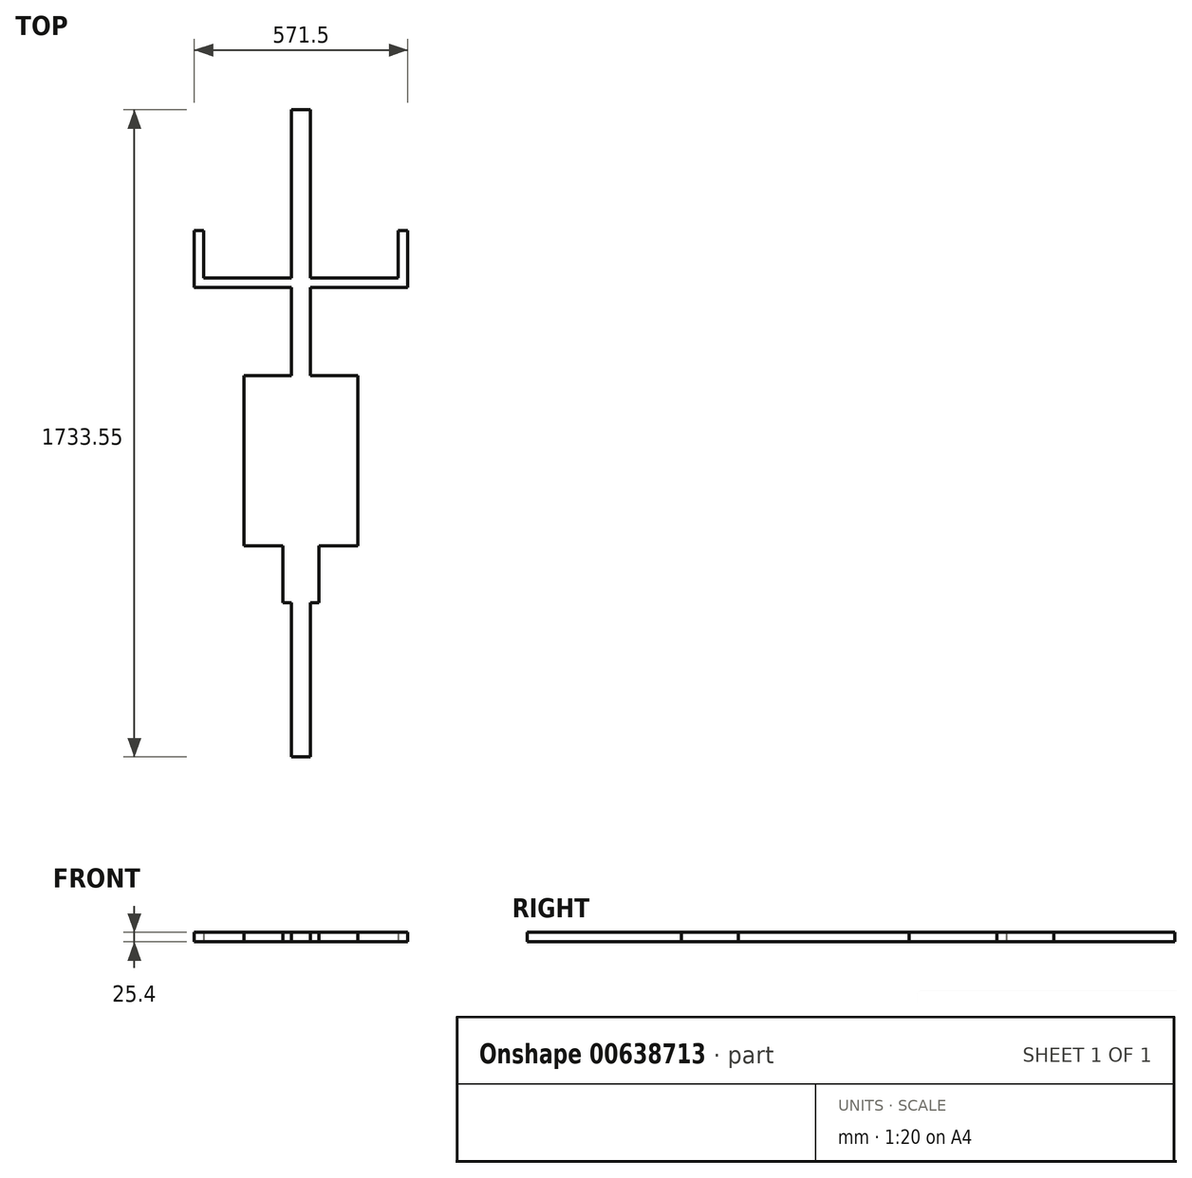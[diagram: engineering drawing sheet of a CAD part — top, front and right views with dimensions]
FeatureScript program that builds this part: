
annotation { "Feature Type Name" : "Feature", "Feature Type Description" : "" }
export const myFeature = defineFeature(function(context is Context, id is Id, definition is map)
    precondition{}
    {
        {
            var Q0;
            Q0=qCreatedBy(makeId("Top.planeOp"),FACE);
            var sketch = newSketch(context, id + "F0", { "sketchPlane" : qUnion([Q0])});
            skLineSegment(sketch, "E0.bottom", {"start": v(-25.4, 0) * mm, "end": v(25.4, 0) * mm});
            skLineSegment(sketch, "E0.top", {"start": v(-25.4, 1733.55) * mm, "end": v(25.4, 1733.55) * mm});
            skLineSegment(sketch, "E0.left", {"start": v(-25.4, 0) * mm, "end": v(-25.4, 1733.55) * mm});
            skLineSegment(sketch, "E0.right", {"start": v(25.4, 0) * mm, "end": v(25.4, 1733.55) * mm});
            skLineSegment(sketch, "E1.bottom", {"start": v(48.57, 412.75) * mm, "end": v(-48.57, 412.75) * mm});
            skLineSegment(sketch, "E1.top", {"start": v(48.57, 634.47) * mm, "end": v(-48.57, 634.47) * mm});
            skLineSegment(sketch, "E1.left", {"start": v(48.57, 412.75) * mm, "end": v(48.57, 634.47) * mm});
            skLineSegment(sketch, "E1.right", {"start": v(-48.57, 412.75) * mm, "end": v(-48.57, 634.47) * mm});
            skPoint(sketch, "E1.middle", {"position": v(0, 523.61) * mm});
            skLineSegment(sketch, "E2.bottom", {"start": v(285.75, 1257.3) * mm, "end": v(-285.75, 1257.3) * mm});
            skLineSegment(sketch, "E2.top", {"start": v(285.75, 1409.7) * mm, "end": v(260.35, 1409.7) * mm});
            skLineSegment(sketch, "E2.left", {"start": v(285.75, 1257.3) * mm, "end": v(285.75, 1409.7) * mm});
            skLineSegment(sketch, "E2.right", {"start": v(-285.75, 1257.3) * mm, "end": v(-285.75, 1409.7) * mm});
            skPoint(sketch, "E2.middle", {"position": v(0, 1333.5) * mm});
            skLineSegment(sketch, "E3.bottom", {"start": v(152.4, 565.15) * mm, "end": v(-152.4, 565.15) * mm});
            skLineSegment(sketch, "E3.top", {"start": v(152.4, 1021.9) * mm, "end": v(-152.4, 1021.9) * mm});
            skLineSegment(sketch, "E3.left", {"start": v(152.4, 565.15) * mm, "end": v(152.4, 1021.9) * mm});
            skLineSegment(sketch, "E3.right", {"start": v(-152.4, 565.15) * mm, "end": v(-152.4, 1021.9) * mm});
            skPoint(sketch, "E3.middle", {"position": v(0, 793.52) * mm});
            skLineSegment(sketch, "E4.bottom", {"start": v(260.35, 1282.7) * mm, "end": v(-260.35, 1282.7) * mm});
            skLineSegment(sketch, "E4.left", {"start": v(260.35, 1282.7) * mm, "end": v(260.35, 1409.7) * mm});
            skLineSegment(sketch, "E4.right", {"start": v(-260.35, 1282.7) * mm, "end": v(-260.35, 1409.7) * mm});
            skLineSegment(sketch, "E5.trimOffspring", {"start": v(-260.35, 1409.7) * mm, "end": v(-285.75, 1409.7) * mm});
            skSolve(sketch);
        }
        {
            var Q0;
            Q0=qSketchRegion(id+"F0",true);
            var Q1;
            {var subQ0=sQuery(id+"F0.wireOp",EDGE,"E3.bottom");var subQ1=sQuery(id+"F0.wireOp",EDGE,"E0.left");var subQ2=makeQuery(id+"F0.imprint","INTERSECT",VERTEX,{"derivedFrom":[subQ1,subQ0]});Q1=makeQuery(id+"F0.imprint","IMPRINT",FACE,{"disambiguationData":[TD([[makeQuery(id+"F0.imprint","IMPRINT",EDGE,{"disambiguationData":[TD([[subQ2,-1.0]])],"derivedFrom":subQ1}),-1.0]])]});}
            extrude(context, id + "F1", {"entities" : qUnion([Q0, Q1]), "depth" : 25.4 * mm, "offsetDistance" : 25.4 * mm});
        }
    });
